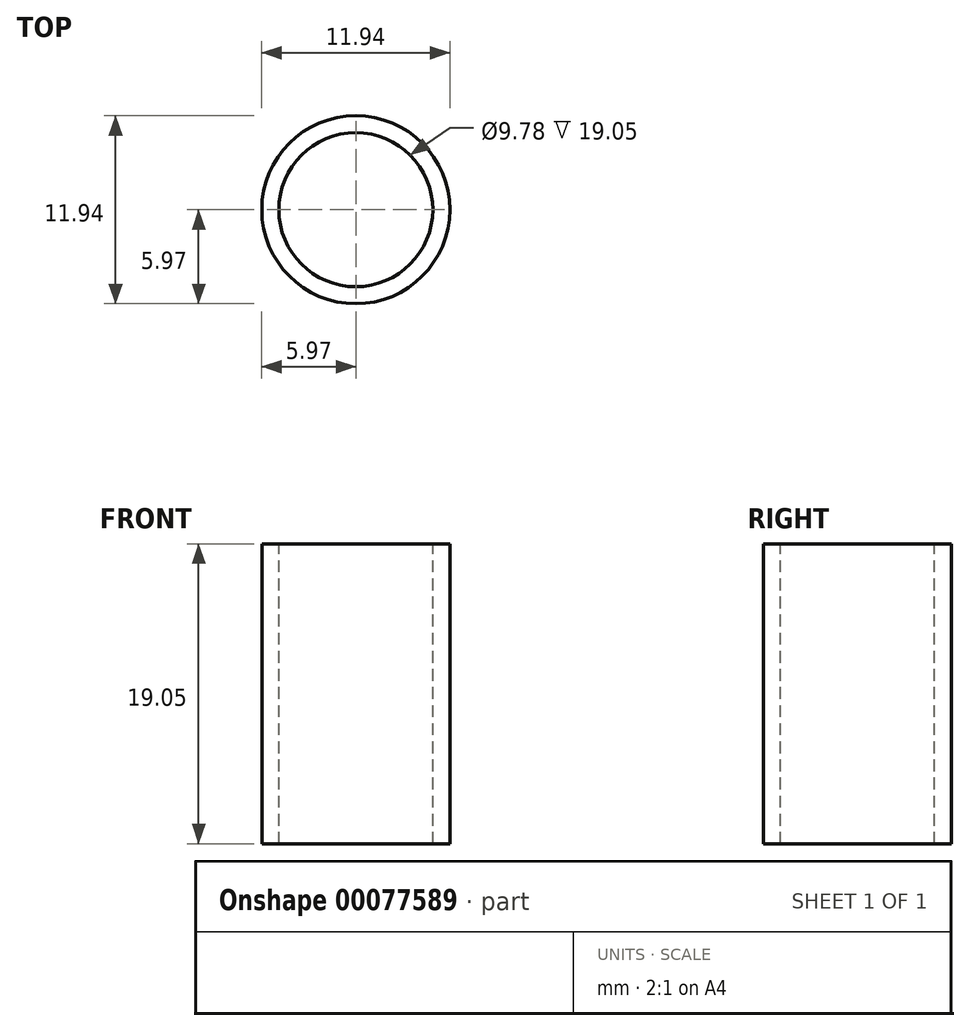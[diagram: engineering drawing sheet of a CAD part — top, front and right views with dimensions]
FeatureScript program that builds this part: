
annotation { "Feature Type Name" : "Feature", "Feature Type Description" : "" }
export const myFeature = defineFeature(function(context is Context, id is Id, definition is map)
    precondition{}
    {
        {
            var Q0;
            Q0=qCreatedBy(makeId("Top.planeOp"),FACE);
            var sketch = newSketch(context, id + "F0", { "sketchPlane" : qUnion([Q0])});
            skCircle(sketch, "E0", {"center": v(0, 0) * mm, "radius": 5.97 * mm});
            skCircle(sketch, "E1", {"center": v(0, 0) * mm, "radius": 4.89 * mm});
            skSolve(sketch);
        }
        {
            var Q0;
            Q0=makeQuery(id+"F0.imprint","IMPRINT",FACE,{"disambiguationData":[TD([[makeQuery(id+"F0.imprint","IMPRINT",EDGE,{"derivedFrom":sQuery(id+"F0.wireOp",EDGE,"E0")}),1.0]])]});
            extrude(context, id + "F1", {"entities" : qUnion([Q0]), "oppositeDirection" : true, "depth" : 19.05 * mm});
        }
        {
            var Q0;
            Q0=makeQuery(id+"F1.opExtrude","SWEPT_BODY",BODY,{"disambiguationData":[OSD([sQuery(id+"F0.wireOp",EDGE,"E0"),sQuery(id+"F0.wireOp",EDGE,"E1")])]});
            transform(context, id + "F2", {"entities" : qUnion([Q0]), "transformType" : TransformType.TRANSLATION_3D, "dx" : 0 * mm, "dy" : 0 * mm, "dz" : 0 * mm, "makeCopy" : true});
        }
        {
            var Q0;
            Q0=makeQuery(id+"F1.opExtrude","SWEPT_BODY",BODY,{"disambiguationData":[OSD([sQuery(id+"F0.wireOp",EDGE,"E0"),sQuery(id+"F0.wireOp",EDGE,"E1")])]});
            deleteBodies(context, id + "F3", {"entities" : qUnion([Q0])});
        }
    });
